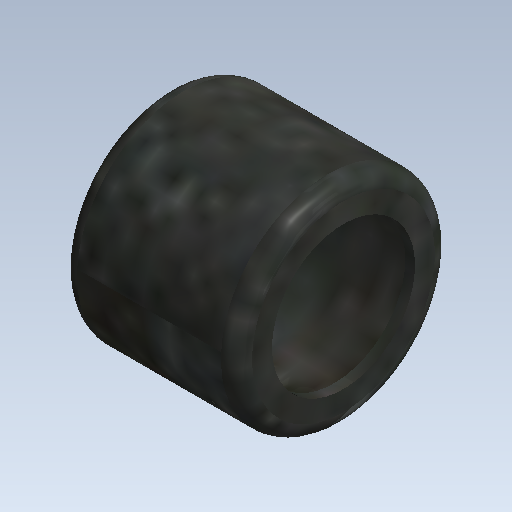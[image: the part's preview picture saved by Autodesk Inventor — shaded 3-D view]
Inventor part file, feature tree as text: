
AUTODESK INVENTOR PART (.ipt)
format: ipt  version: 2021 (Build 250183000, 183)  size: 212,480 bytes
history: native  units: mm (DEFAULTED — no unit token found)
features: other x21, revolve x1, sketch x1
ambient origin geometry x8: Origin, YZ Plane, XZ Plane, XY Plane, X Axis, Y Axis, Z Axis, Center Point
bodies: Solid1 (feature_tree)
feature tree (23):
  revolve  "Revolution1"  [1 undecoded]
  other  "IP_1_XY"
  other  "IP_1_YZ"
  other  "IP_1_ZX"
  other  "IP_1_X"
  other  "IP_1_Y"
  other  "IP_1_Z"
  other  "IP_1_Center"
  other  "IP_5_XY"
  other  "IP_5_YZ"
  other  "IP_5_ZX"
  other  "IP_5_X"
  other  "IP_5_Y"
  other  "IP_5_Z"
  other  "IP_5_Center"
  other  "IP_6_XY"
  other  "IP_6_YZ"
  other  "IP_6_ZX"
  other  "IP_6_X"
  other  "IP_6_Y"
  other  "IP_6_Z"
  other  "IP_6_Center"
  sketch  "Sketch_1"  dims[d0=360.0deg d1=0.0mm]
note: 1 required parameter value undecoded (feature->parameter linkage not recoverable at this tier; creation-order binding heuristic only, values carry confidence <= 0.55)
